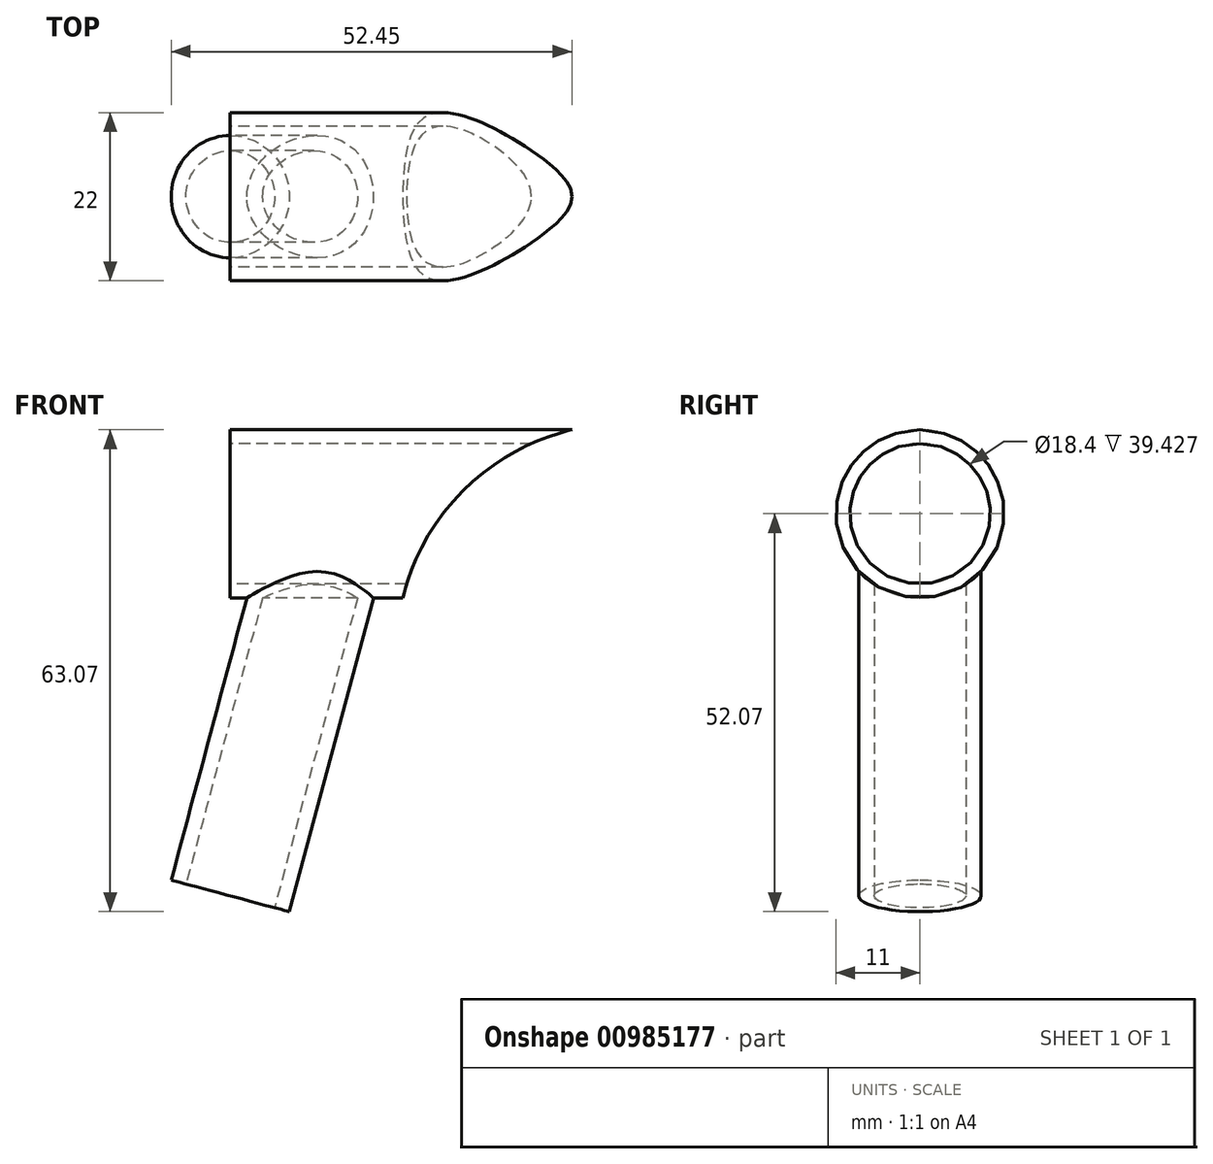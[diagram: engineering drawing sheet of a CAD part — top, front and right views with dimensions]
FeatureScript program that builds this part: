
annotation { "Feature Type Name" : "Feature", "Feature Type Description" : "" }
export const myFeature = defineFeature(function(context is Context, id is Id, definition is map)
    precondition{}
    {
        {
            var Q0;
            Q0=qCreatedBy(makeId("Front.planeOp"),FACE);
            var sketch = newSketch(context, id + "F0", { "sketchPlane" : qUnion([Q0])});
            skLineSegment(sketch, "E0", {"start": v(0, 0) * mm, "end": v(44.5, -11.93) * mm});
            skLineSegment(sketch, "E1", {"start": v(0, 0) * mm, "end": v(43.14, 0) * mm});
            skSolve(sketch);
        }
        {
            var Q0;
            Q0=qCreatedBy(makeId("Top.planeOp"),FACE);
            var sketch = newSketch(context, id + "F1", { "sketchPlane" : qUnion([Q0])});
            skLineSegment(sketch, "E2", {"start": v(0, 0) * mm, "end": v(0, -70.88) * mm});
            skSolve(sketch);
        }
        {
            var Q0;
            Q0=sQuery(id+"F1.wireOp",VERTEX,"E2.end");
            var Q1;
            Q1=sQuery(id+"F0.wireOp",VERTEX,"E0.end");
            var Q2;
            Q2=sQuery(id+"F0.wireOp",VERTEX,"E0.start");
            cPlane(context, id + "F2", {"entities" : qUnion([Q0, Q1, Q2]), "cplaneType" : CPlaneType.THREE_POINT, "offset" : 25 * mm, "width" : 150 * mm, "height" : 150 * mm});
        }
        {
            var Q0;
            Q0=qCreatedBy(id+"F2.planeOp",FACE);
            var sketch = newSketch(context, id + "F3", { "sketchPlane" : qUnion([Q0])});
            skCircle(sketch, "E3", {"center": v(0, 0) * mm, "radius": 6 * mm});
            skCircle(sketch, "E4", {"center": v(0, 0) * mm, "radius": 8 * mm});
            skSolve(sketch);
        }
        {
            var Q0;
            Q0=makeQuery(id+"F3.imprint","IMPRINT",FACE,{"disambiguationData":[TD([[makeQuery(id+"F3.imprint","IMPRINT",EDGE,{"derivedFrom":sQuery(id+"F3.wireOp",EDGE,"E3")}),-1.0]])]});
            extrude(context, id + "F4", {"entities" : qUnion([Q0]), "oppositeDirection" : true, "depth" : 50 * mm, "offsetDistance" : 25 * mm});
        }
        {
            var Q0;
            Q0=qCreatedBy(makeId("Right.planeOp"),FACE);
            var sketch = newSketch(context, id + "F5", { "sketchPlane" : qUnion([Q0])});
            skCircle(sketch, "E5", {"center": v(0, 50) * mm, "radius": 9.2 * mm});
            skCircle(sketch, "E6", {"center": v(0, 50) * mm, "radius": 11 * mm});
            skSolve(sketch);
        }
        {
            var Q0;
            Q0=makeQuery(id+"F5.imprint","IMPRINT",FACE,{"disambiguationData":[TD([[makeQuery(id+"F5.imprint","IMPRINT",EDGE,{"derivedFrom":sQuery(id+"F5.wireOp",EDGE,"E5")}),-1.0]])]});
            extrude(context, id + "F6", {"entities" : qUnion([Q0]), "operationType" : NewBodyOperationType.ADD, "depth" : 50 * mm, "offsetDistance" : 25 * mm});
        }
        {
            var Q0;
            Q0=makeQuery(id+"F6.opExtrude","CAP_FACE",FACE,{"disambiguationData":[OSD([sQuery(id+"F5.wireOp",EDGE,"E5"),sQuery(id+"F5.wireOp",EDGE,"E6")])],"isStart":false});
            var sketch = newSketch(context, id + "F7", { "sketchPlane" : qUnion([Q0])});
            skCircle(sketch, "E7", {"center": v(0, 50) * mm, "radius": 9.2 * mm});
            skSolve(sketch);
        }
        {
            var Q0;
            Q0=makeQuery(id+"F7.imprint","IMPRINT",FACE,{"disambiguationData":[TD([[makeQuery(id+"F7.imprint","IMPRINT",EDGE,{"derivedFrom":sQuery(id+"F7.wireOp",EDGE,"E7")}),1.0]])]});
            extrude(context, id + "F8", {"entities" : qUnion([Q0]), "operationType" : NewBodyOperationType.REMOVE, "endBound" : BoundingType.THROUGH_ALL, "oppositeDirection" : true, "depth" : 25 * mm, "offsetDistance" : 25 * mm});
        }
        {
            var Q0;
            Q0=qCreatedBy(makeId("Front.planeOp"),FACE);
            var sketch = newSketch(context, id + "F9", { "sketchPlane" : qUnion([Q0])});
            skCircle(sketch, "E8", {"center": v(51.68, 31.85) * mm, "radius": 29.97 * mm});
            skSolve(sketch);
        }
        {
            var Q0;
            Q0=makeQuery(id+"F9.imprint","IMPRINT",FACE,{"disambiguationData":[TD([[makeQuery(id+"F9.imprint","IMPRINT",EDGE,{"derivedFrom":sQuery(id+"F9.wireOp",EDGE,"E8")}),1.0]])]});
            extrude(context, id + "F10", {"entities" : qUnion([Q0]), "operationType" : NewBodyOperationType.REMOVE, "endBound" : BoundingType.SYMMETRIC, "oppositeDirection" : true, "depth" : 25 * mm, "offsetDistance" : 25 * mm});
        }
    });
